# Revit family: 511_3V_PW_nailfin
name_source: partatom
category: Windows
revit_build: Autodesk Revit 2016 (Build: 20150220_1215(x64)
units: mm (PartAtom-declared; Revit-internal decimal feet)

## family parameters
Always vertical = Yes
Cut with Voids When Loaded = No
Host = Wall
OmniClass Number = 23.30.20.00
OmniClass Title = Windows
Room Calculation Point = No
Shared = No

## types (126) — shared parameters
Default Sill Height = 31 1/2"
Wall Closure = By host

## per-type parameters (varying)
| type | Bar set | Bar set2 | Height | MLW | Width |
| 36x72 | 48" | 24" | 72" | 3" | 36" |
| 24x48 | 32" | 16" | 48" | 2" | 24" |
| 12x36Min | 24" | 12" | 36" | 1 1/2" | 12" |
| 72x120Max | 80" | 40" | 120" | 5" | 72" |
| 48x120 | 80" | 40" | 120" | 5" | 48" |
| 60x120 | 80" | 40" | 120" | 5" | 60" |
| 12x42 | 28" | 14" | 42" | 1 3/4" | 12" |
| 12x48 | 32" | 16" | 48" | 2" | 12" |
| 12x54 | 36" | 18" | 54" | 2 1/4" | 12" |
| 12x60 | 40" | 20" | 60" | 2 1/2" | 12" |
| 12x66 | 44" | 22" | 66" | 2 3/4" | 12" |
| 18x36 | 24" | 12" | 36" | 1 1/2" | 18" |
| 18x42 | 28" | 14" | 42" | 1 3/4" | 18" |
| 18x48 | 32" | 16" | 48" | 2" | 18" |
| 18x54 | 36" | 18" | 54" | 2 1/4" | 18" |
| 18x84 | 56" | 28" | 84" | 3 1/2" | 18" |
| 18x60 | 40" | 20" | 60" | 2 1/2" | 18" |
| 18x66 | 44" | 22" | 66" | 2 3/4" | 18" |
| 18x72 | 48" | 24" | 72" | 3" | 18" |
| 18x78 | 52" | 26" | 78" | 3 1/4" | 18" |
| 24x36 | 24" | 12" | 36" | 1 1/2" | 24" |
| 24x42 | 28" | 14" | 42" | 1 3/4" | 24" |
| 24x54 | 36" | 18" | 54" | 2 1/4" | 24" |
| 24x72 | 48" | 24" | 72" | 3" | 24" |
| 24x102 | 68" | 34" | 102" | 4 1/4" | 24" |
| 24x60 | 40" | 20" | 60" | 2 1/2" | 24" |
| 24x66 | 44" | 22" | 66" | 2 3/4" | 24" |
| 24x78 | 52" | 26" | 78" | 3 1/4" | 24" |
| 24x84 | 56" | 28" | 84" | 3 1/2" | 24" |
| 24x90 | 60" | 30" | 90" | 3 3/4" | 24" |
| 24x96 | 64" | 32" | 96" | 4" | 24" |
| 30x36 | 24" | 12" | 36" | 1 1/2" | 30" |
| 30x108 | 72" | 36" | 108" | 4 1/2" | 30" |
| 30x120 | 80" | 40" | 120" | 5" | 30" |
| 30x42 | 28" | 14" | 42" | 1 3/4" | 30" |
| 30x48 | 32" | 16" | 48" | 2" | 30" |
| 30x54 | 36" | 18" | 54" | 2 1/4" | 30" |
| 30x60 | 40" | 20" | 60" | 2 1/2" | 30" |
| 30x66 | 44" | 22" | 66" | 2 3/4" | 30" |
| 30x72 | 48" | 24" | 72" | 3" | 30" |
| 30x78 | 52" | 26" | 78" | 3 1/4" | 30" |
| 30x84 | 56" | 28" | 84" | 3 1/2" | 30" |
| 30x90 | 60" | 30" | 90" | 3 3/4" | 30" |
| 30x96 | 64" | 32" | 96" | 4" | 30" |
| 30x102 | 68" | 34" | 102" | 4 1/4" | 30" |
| 30x114 | 76" | 38" | 114" | 4 3/4" | 30" |
| 36x36 | 24" | 12" | 36" | 1 1/2" | 36" |
| 36x42 | 28" | 14" | 42" | 1 3/4" | 36" |
| 36x48 | 32" | 16" | 48" | 2" | 36" |
| 36x54 | 36" | 18" | 54" | 2 1/4" | 36" |
| 36x60 | 40" | 20" | 60" | 2 1/2" | 36" |
| 36x66 | 44" | 22" | 66" | 2 3/4" | 36" |
| 36x78 | 52" | 26" | 78" | 3 1/4" | 36" |
| 36x84 | 56" | 28" | 84" | 3 1/2" | 36" |
| 36x90 | 60" | 30" | 90" | 3 3/4" | 36" |
| 36x96 | 64" | 32" | 96" | 4" | 36" |
| 36x102 | 68" | 34" | 102" | 4 1/4" | 36" |
| 36x108 | 72" | 36" | 108" | 4 1/2" | 36" |
| 36x114 | 76" | 38" | 114" | 4 3/4" | 36" |
| 36x120 | 80" | 40" | 120" | 5" | 36" |
| 42x42 | 28" | 14" | 42" | 1 3/4" | 42" |
| 42x48 | 32" | 16" | 48" | 2" | 42" |
| 42x54 | 36" | 18" | 54" | 2 1/4" | 42" |
| 42x60 | 40" | 20" | 60" | 2 1/2" | 42" |
| 42x66 | 44" | 22" | 66" | 2 3/4" | 42" |
| 42x72 | 48" | 24" | 72" | 3" | 42" |
| 42x78 | 52" | 26" | 78" | 3 1/4" | 42" |
| 42x84 | 56" | 28" | 84" | 3 1/2" | 42" |
| 42x90 | 60" | 30" | 90" | 3 3/4" | 42" |
| 42x96 | 64" | 32" | 96" | 4" | 42" |
| 42x102 | 68" | 34" | 102" | 4 1/4" | 42" |
| 42x108 | 72" | 36" | 108" | 4 1/2" | 42" |
| 42x114 | 76" | 38" | 114" | 4 3/4" | 42" |
| 42x120 | 80" | 40" | 120" | 5" | 42" |
| 48x48 | 32" | 16" | 48" | 2" | 48" |
| 48x54 | 36" | 18" | 54" | 2 1/4" | 48" |
| 48x60 | 40" | 20" | 60" | 2 1/2" | 48" |
| 48x66 | 44" | 22" | 66" | 2 3/4" | 48" |
| 48x72 | 48" | 24" | 72" | 3" | 48" |
| 48x78 | 52" | 26" | 78" | 3 1/4" | 48" |
| 48x84 | 56" | 28" | 84" | 3 1/2" | 48" |
| 48x90 | 60" | 30" | 90" | 3 3/4" | 48" |
| 48x96 | 64" | 32" | 96" | 4" | 48" |
| 48x102 | 68" | 34" | 102" | 4 1/4" | 48" |
| 48x108 | 72" | 36" | 108" | 4 1/2" | 48" |
| 48x114 | 76" | 38" | 114" | 4 3/4" | 48" |
| 54x54 | 36" | 18" | 54" | 2 1/4" | 54" |
| 54x60 | 40" | 20" | 60" | 2 1/2" | 54" |
| 54x66 | 44" | 22" | 66" | 2 3/4" | 54" |
| 54x72 | 48" | 24" | 72" | 3" | 54" |
| 54x78 | 52" | 26" | 78" | 3 1/4" | 54" |
| 54x84 | 56" | 28" | 84" | 3 1/2" | 54" |
| 54x90 | 60" | 30" | 90" | 3 3/4" | 54" |
| 54x96 | 64" | 32" | 96" | 4" | 54" |
| 54x102 | 68" | 34" | 102" | 4 1/4" | 54" |
| 54x108 | 72" | 36" | 108" | 4 1/2" | 54" |
| 54x114 | 76" | 38" | 114" | 4 3/4" | 54" |
| 54x120 | 80" | 40" | 120" | 5" | 54" |
| 60x60 | 40" | 20" | 60" | 2 1/2" | 60" |
| 60x66 | 44" | 22" | 66" | 2 3/4" | 60" |
| 60x72 | 48" | 24" | 72" | 3" | 60" |
| 60x78 | 52" | 26" | 78" | 3 1/4" | 60" |
| 60x84 | 56" | 28" | 84" | 3 1/2" | 60" |
| 60x90 | 60" | 30" | 90" | 3 3/4" | 60" |
| 60x96 | 64" | 32" | 96" | 4" | 60" |
| 60x102 | 68" | 34" | 102" | 4 1/4" | 60" |
| 60x108 | 72" | 36" | 108" | 4 1/2" | 60" |
| 60x114 | 76" | 38" | 114" | 4 3/4" | 60" |
| 66x66 | 44" | 22" | 66" | 2 3/4" | 66" |
| 66x72 | 48" | 24" | 72" | 3" | 66" |
| 66x78 | 52" | 26" | 78" | 3 1/4" | 66" |
| 66x84 | 56" | 28" | 84" | 3 1/2" | 66" |
| 66x90 | 60" | 30" | 90" | 3 3/4" | 66" |
| 66x96 | 64" | 32" | 96" | 4" | 66" |
| 66x102 | 68" | 34" | 102" | 4 1/4" | 66" |
| 66x108 | 72" | 36" | 108" | 4 1/2" | 66" |
| 66x114 | 76" | 38" | 114" | 4 3/4" | 66" |
| 66x120 | 80" | 40" | 120" | 5" | 66" |
| 72x72 | 48" | 24" | 72" | 3" | 72" |
| 72x78 | 52" | 26" | 78" | 3 1/4" | 72" |
| 72x84 | 56" | 28" | 84" | 3 1/2" | 72" |
| 72x90 | 60" | 30" | 90" | 3 3/4" | 72" |
| 72x96 | 64" | 32" | 96" | 4" | 72" |
| 72x102 | 68" | 34" | 102" | 4 1/4" | 72" |
| 72x108 | 72" | 36" | 108" | 4 1/2" | 72" |
| 72x114 | 76" | 38" | 114" | 4 3/4" | 72" |

## geometry (parser evidence)
native form markers: Sweep x3
no freeform markers — native parametric forms only
